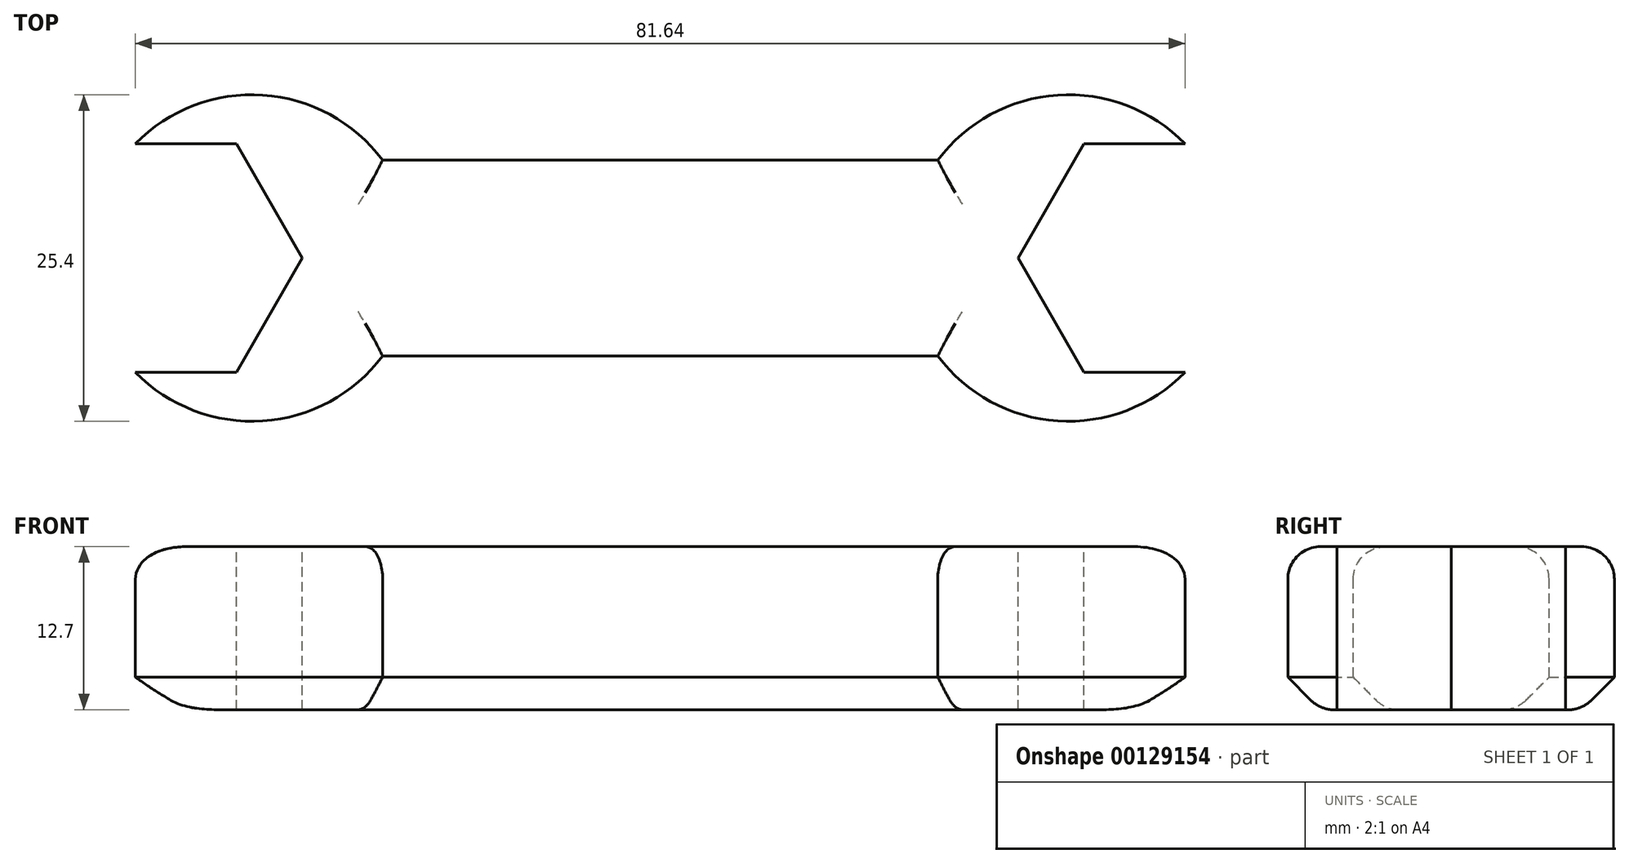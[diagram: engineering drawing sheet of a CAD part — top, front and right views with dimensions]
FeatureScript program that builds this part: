
annotation { "Feature Type Name" : "Feature", "Feature Type Description" : "" }
export const myFeature = defineFeature(function(context is Context, id is Id, definition is map)
    precondition{}
    {
        {
            var Q0;
            Q0=qCreatedBy(makeId("Top.planeOp"),FACE);
            var sketch = newSketch(context, id + "F0", { "sketchPlane" : qUnion([Q0])});
            skArc(sketch, "E0", {"start": v(-21.59, 7.62) * mm, "mid": v(-44.45, 0) * mm, "end": v(-21.59, -7.62) * mm});
            skArc(sketch, "E1", {"start": v(21.59, -7.62) * mm, "mid": v(44.45, 0) * mm, "end": v(21.59, 7.62) * mm});
            skLineSegment(sketch, "E2", {"start": v(-21.59, 7.62) * mm, "end": v(21.59, 7.62) * mm});
            skLineSegment(sketch, "E3", {"start": v(-21.59, -7.62) * mm, "end": v(21.59, -7.62) * mm});
            skLineSegment(sketch, "E4", {"start": v(-31.75, 0) * mm, "end": v(31.75, 0) * mm, "construction": true});
            skSolve(sketch);
        }
        {
            var Q0;
            Q0 = qSketchRegion(id + "F0", true);
            extrude(context, id + "F1", {"entities" : qUnion([Q0]), "endBound" : BoundingType.SYMMETRIC, "oppositeDirection" : true, "depth" : 12.7 * mm});
        }
        {
            var Q0;
            Q0=makeQuery(id+"F1.opExtrude","CAP_FACE",FACE,{"disambiguationData":[OSD([sQuery(id+"F0.wireOp",EDGE,"E0"),sQuery(id+"F0.wireOp",EDGE,"E1"),sQuery(id+"F0.wireOp",EDGE,"E2"),sQuery(id+"F0.wireOp",EDGE,"E3")])],"isStart":true});
            var sketch = newSketch(context, id + "F2", { "sketchPlane" : qUnion([Q0])});
            skCircle(sketch, "E5.cCircle", {"center": v(-38.1, 0) * mm, "radius": 8.9 * mm, "construction": true});
            skLineSegment(sketch, "E5.0", {"start": v(-32.97, 8.9) * mm, "end": v(-27.83, 0) * mm});
            skLineSegment(sketch, "E5.1", {"start": v(-27.83, 0) * mm, "end": v(-32.97, -8.89) * mm});
            skLineSegment(sketch, "E5.2", {"start": v(-32.97, -8.89) * mm, "end": v(-43.23, -8.89) * mm});
            skLineSegment(sketch, "E5.3", {"start": v(-43.23, -8.89) * mm, "end": v(-48.37, 0) * mm});
            skLineSegment(sketch, "E5.4", {"start": v(-48.37, 0) * mm, "end": v(-43.23, 8.89) * mm});
            skLineSegment(sketch, "E5.5", {"start": v(-43.23, 8.89) * mm, "end": v(-32.97, 8.89) * mm});
            skPoint(sketch, "E5.0.midPoint", {"position": v(-29.21, 0) * mm});
            skSolve(sketch);
        }
        {
            var Q0;
            Q0 = qSketchRegion(id + "F2", true);
            extrude(context, id + "F3", {"entities" : qUnion([Q0]), "endBound" : BoundingType.THROUGH_ALL, "oppositeDirection" : true, "depth" : 25.4 * mm});
        }
        {
            var Q0;
            Q0=makeQuery(id+"F3.opExtrude","SWEPT_BODY",BODY,{"disambiguationData":[OSD([sQuery(id+"F2.wireOp",EDGE,"E5.0"),sQuery(id+"F2.wireOp",EDGE,"E5.1"),sQuery(id+"F2.wireOp",EDGE,"E5.2"),sQuery(id+"F2.wireOp",EDGE,"E5.3"),sQuery(id+"F2.wireOp",EDGE,"E5.4"),sQuery(id+"F2.wireOp",EDGE,"E5.5")])]});
            var Q1;
            Q1=qCreatedBy(makeId("Right.planeOp"),FACE);
            mirror(context, id + "F4", {"operationType" : NewBodyOperationType.REMOVE, "entities" : qUnion([Q0]), "mirrorPlane" : qUnion([Q1])});
        }
        {
            var Q0;
            Q0=makeQuery(id+"F3.opExtrude","SWEPT_BODY",BODY,{"disambiguationData":[OSD([sQuery(id+"F2.wireOp",EDGE,"E5.0"),sQuery(id+"F2.wireOp",EDGE,"E5.1"),sQuery(id+"F2.wireOp",EDGE,"E5.2"),sQuery(id+"F2.wireOp",EDGE,"E5.3"),sQuery(id+"F2.wireOp",EDGE,"E5.4"),sQuery(id+"F2.wireOp",EDGE,"E5.5")])]});
            var Q1;
            Q1=makeQuery(id+"F1.opExtrude","SWEPT_BODY",BODY,{"disambiguationData":[OSD([sQuery(id+"F0.wireOp",EDGE,"E0"),sQuery(id+"F0.wireOp",EDGE,"E1"),sQuery(id+"F0.wireOp",EDGE,"E2"),sQuery(id+"F0.wireOp",EDGE,"E3")])]});
            booleanBodies(context, id + "F5", {"operationType" : BooleanOperationType.SUBTRACTION, "tools" : qUnion([Q0]), "targets" : qUnion([Q1])});
        }
        {
            var Q0;
            Q0=makeQuery(id+"F1.opExtrude","CAP_EDGE",EDGE,{"disambiguationData":[OSD([sQuery(id+"F0.wireOp",EDGE,"E3")])],"isStart":true});
            var Q1;
            {var subQ0=sQuery(id+"F0.wireOp",EDGE,"E0");var subQ1=sQuery(id+"F0.wireOp",EDGE,"E3");Q1=makeQuery(id+"F5.opBoolean","SPLIT",EDGE,{"disambiguationData":[TD([makeQuery(id+"F1.opExtrude","SWEPT_FACE",FACE,{"disambiguationData":[OSD([subQ1])]})])],"derivedFrom":makeQuery(id+"F1.opExtrude","CAP_EDGE",EDGE,{"disambiguationData":[OSD([subQ0])],"isStart":true})});}
            var Q2;
            {var subQ0=sQuery(id+"F0.wireOp",EDGE,"E0");var subQ1=sQuery(id+"F0.wireOp",EDGE,"E2");Q2=makeQuery(id+"F5.opBoolean","SPLIT",EDGE,{"disambiguationData":[TD([makeQuery(id+"F1.opExtrude","SWEPT_FACE",FACE,{"disambiguationData":[OSD([subQ1])]})])],"derivedFrom":makeQuery(id+"F1.opExtrude","CAP_EDGE",EDGE,{"disambiguationData":[OSD([subQ0])],"isStart":true})});}
            var Q3;
            Q3=makeQuery(id+"F1.opExtrude","CAP_EDGE",EDGE,{"disambiguationData":[OSD([sQuery(id+"F0.wireOp",EDGE,"E2")])],"isStart":true});
            var Q4;
            {var subQ0=sQuery(id+"F0.wireOp",EDGE,"E2");var subQ1=sQuery(id+"F0.wireOp",EDGE,"E1");Q4=makeQuery(id+"F4.boolean.opBoolean","SPLIT",EDGE,{"disambiguationData":[TD([makeQuery(id+"F1.opExtrude","SWEPT_FACE",FACE,{"disambiguationData":[OSD([subQ0])]})])],"derivedFrom":makeQuery(id+"F1.opExtrude","CAP_EDGE",EDGE,{"disambiguationData":[OSD([subQ1])],"isStart":true})});}
            var Q5;
            {var subQ0=sQuery(id+"F0.wireOp",EDGE,"E3");var subQ1=sQuery(id+"F0.wireOp",EDGE,"E1");Q5=makeQuery(id+"F4.boolean.opBoolean","SPLIT",EDGE,{"disambiguationData":[TD([makeQuery(id+"F1.opExtrude","SWEPT_FACE",FACE,{"disambiguationData":[OSD([subQ0])]})])],"derivedFrom":makeQuery(id+"F1.opExtrude","CAP_EDGE",EDGE,{"disambiguationData":[OSD([subQ1])],"isStart":true})});}
            fillet(context, id + "F6", {"entities" : qUnion([Q0, Q1, Q2, Q3, Q4, Q5]), "radius" : 2.54 * mm, "tangentPropagation" : true, "allowEdgeOverflow" : false});
        }
        {
            var Q0;
            {var subQ0=sQuery(id+"F0.wireOp",EDGE,"E0");var subQ1=sQuery(id+"F0.wireOp",EDGE,"E3");Q0=makeQuery(id+"F5.opBoolean","SPLIT",EDGE,{"disambiguationData":[TD([makeQuery(id+"F1.opExtrude","SWEPT_FACE",FACE,{"disambiguationData":[OSD([subQ1])]})])],"derivedFrom":makeQuery(id+"F1.opExtrude","CAP_EDGE",EDGE,{"disambiguationData":[OSD([subQ0])],"isStart":false})});}
            var Q1;
            Q1=makeQuery(id+"F1.opExtrude","CAP_EDGE",EDGE,{"disambiguationData":[OSD([sQuery(id+"F0.wireOp",EDGE,"E3")])],"isStart":false});
            var Q2;
            {var subQ0=sQuery(id+"F0.wireOp",EDGE,"E3");var subQ1=sQuery(id+"F0.wireOp",EDGE,"E1");Q2=makeQuery(id+"F4.boolean.opBoolean","SPLIT",EDGE,{"disambiguationData":[TD([makeQuery(id+"F1.opExtrude","SWEPT_FACE",FACE,{"disambiguationData":[OSD([subQ0])]})])],"derivedFrom":makeQuery(id+"F1.opExtrude","CAP_EDGE",EDGE,{"disambiguationData":[OSD([subQ1])],"isStart":false})});}
            var Q3;
            {var subQ0=sQuery(id+"F0.wireOp",EDGE,"E2");var subQ1=sQuery(id+"F0.wireOp",EDGE,"E1");Q3=makeQuery(id+"F4.boolean.opBoolean","SPLIT",EDGE,{"disambiguationData":[TD([makeQuery(id+"F1.opExtrude","SWEPT_FACE",FACE,{"disambiguationData":[OSD([subQ0])]})])],"derivedFrom":makeQuery(id+"F1.opExtrude","CAP_EDGE",EDGE,{"disambiguationData":[OSD([subQ1])],"isStart":false})});}
            var Q4;
            Q4=makeQuery(id+"F1.opExtrude","CAP_EDGE",EDGE,{"disambiguationData":[OSD([sQuery(id+"F0.wireOp",EDGE,"E2")])],"isStart":false});
            var Q5;
            {var subQ0=sQuery(id+"F0.wireOp",EDGE,"E0");var subQ1=sQuery(id+"F0.wireOp",EDGE,"E2");Q5=makeQuery(id+"F5.opBoolean","SPLIT",EDGE,{"disambiguationData":[TD([makeQuery(id+"F1.opExtrude","SWEPT_FACE",FACE,{"disambiguationData":[OSD([subQ1])]})])],"derivedFrom":makeQuery(id+"F1.opExtrude","CAP_EDGE",EDGE,{"disambiguationData":[OSD([subQ0])],"isStart":false})});}
            chamfer(context, id + "F7", {"entities" : qUnion([Q0, Q1, Q2, Q3, Q4, Q5]), "width" : 2.54 * mm, "tangentPropagation" : true});
        }
        {
            var Q0;
            {var subQ0=sQuery(id+"F0.wireOp",EDGE,"E3");var subQ1=sQuery(id+"F0.wireOp",EDGE,"E0");var subQ2=makeQuery(id+"F1.opExtrude","CAP_FACE",FACE,{"disambiguationData":[OSD([subQ1,sQuery(id+"F0.wireOp",EDGE,"E1"),sQuery(id+"F0.wireOp",EDGE,"E2"),subQ0])],"isStart":false});Q0=makeQuery(id+"F7.opChamfer","BLEND_EDGE",EDGE,{"blendedFrom":[makeQuery(id+"F5.opBoolean","SPLIT",EDGE,{"disambiguationData":[TD([makeQuery(id+"F1.opExtrude","SWEPT_FACE",FACE,{"disambiguationData":[OSD([subQ0])]})])],"derivedFrom":makeQuery(id+"F1.opExtrude","CAP_EDGE",EDGE,{"disambiguationData":[OSD([subQ1])],"isStart":false})}),subQ2],"blendedInto":[subQ2]});}
            var Q1;
            {var subQ0=sQuery(id+"F0.wireOp",EDGE,"E3");Q1=makeQuery(id+"F7.opChamfer","BLEND_EDGE",EDGE,{"blendedFrom":[makeQuery(id+"F1.opExtrude","CAP_EDGE",EDGE,{"disambiguationData":[OSD([subQ0])],"isStart":false}),makeQuery(id+"F1.opExtrude","CAP_FACE",FACE,{"disambiguationData":[OSD([sQuery(id+"F0.wireOp",EDGE,"E0"),sQuery(id+"F0.wireOp",EDGE,"E1"),sQuery(id+"F0.wireOp",EDGE,"E2"),subQ0])],"isStart":false})],"blendedInto":[makeQuery(id+"F1.opExtrude","CAP_FACE",FACE,{"disambiguationData":[OSD([sQuery(id+"F0.wireOp",EDGE,"E0"),sQuery(id+"F0.wireOp",EDGE,"E1"),sQuery(id+"F0.wireOp",EDGE,"E2"),subQ0])],"isStart":false})]});}
            var Q2;
            {var subQ0=sQuery(id+"F0.wireOp",EDGE,"E3");var subQ1=sQuery(id+"F0.wireOp",EDGE,"E1");var subQ2=makeQuery(id+"F1.opExtrude","CAP_FACE",FACE,{"disambiguationData":[OSD([sQuery(id+"F0.wireOp",EDGE,"E0"),subQ1,sQuery(id+"F0.wireOp",EDGE,"E2"),subQ0])],"isStart":false});Q2=makeQuery(id+"F7.opChamfer","BLEND_EDGE",EDGE,{"blendedFrom":[makeQuery(id+"F4.boolean.opBoolean","SPLIT",EDGE,{"disambiguationData":[TD([makeQuery(id+"F1.opExtrude","SWEPT_FACE",FACE,{"disambiguationData":[OSD([subQ0])]})])],"derivedFrom":makeQuery(id+"F1.opExtrude","CAP_EDGE",EDGE,{"disambiguationData":[OSD([subQ1])],"isStart":false})}),subQ2],"blendedInto":[subQ2]});}
            var Q3;
            {var subQ0=sQuery(id+"F0.wireOp",EDGE,"E2");var subQ1=sQuery(id+"F0.wireOp",EDGE,"E1");var subQ2=makeQuery(id+"F1.opExtrude","CAP_FACE",FACE,{"disambiguationData":[OSD([sQuery(id+"F0.wireOp",EDGE,"E0"),subQ1,subQ0,sQuery(id+"F0.wireOp",EDGE,"E3")])],"isStart":false});Q3=makeQuery(id+"F7.opChamfer","BLEND_EDGE",EDGE,{"blendedFrom":[makeQuery(id+"F4.boolean.opBoolean","SPLIT",EDGE,{"disambiguationData":[TD([makeQuery(id+"F1.opExtrude","SWEPT_FACE",FACE,{"disambiguationData":[OSD([subQ0])]})])],"derivedFrom":makeQuery(id+"F1.opExtrude","CAP_EDGE",EDGE,{"disambiguationData":[OSD([subQ1])],"isStart":false})}),subQ2],"blendedInto":[subQ2]});}
            var Q4;
            {var subQ0=sQuery(id+"F0.wireOp",EDGE,"E2");Q4=makeQuery(id+"F7.opChamfer","BLEND_EDGE",EDGE,{"blendedFrom":[makeQuery(id+"F1.opExtrude","CAP_EDGE",EDGE,{"disambiguationData":[OSD([subQ0])],"isStart":false}),makeQuery(id+"F1.opExtrude","CAP_FACE",FACE,{"disambiguationData":[OSD([sQuery(id+"F0.wireOp",EDGE,"E0"),sQuery(id+"F0.wireOp",EDGE,"E1"),subQ0,sQuery(id+"F0.wireOp",EDGE,"E3")])],"isStart":false})],"blendedInto":[makeQuery(id+"F1.opExtrude","CAP_FACE",FACE,{"disambiguationData":[OSD([sQuery(id+"F0.wireOp",EDGE,"E0"),sQuery(id+"F0.wireOp",EDGE,"E1"),subQ0,sQuery(id+"F0.wireOp",EDGE,"E3")])],"isStart":false})]});}
            var Q5;
            {var subQ0=sQuery(id+"F0.wireOp",EDGE,"E2");var subQ1=sQuery(id+"F0.wireOp",EDGE,"E0");var subQ2=makeQuery(id+"F1.opExtrude","CAP_FACE",FACE,{"disambiguationData":[OSD([subQ1,sQuery(id+"F0.wireOp",EDGE,"E1"),subQ0,sQuery(id+"F0.wireOp",EDGE,"E3")])],"isStart":false});Q5=makeQuery(id+"F7.opChamfer","BLEND_EDGE",EDGE,{"blendedFrom":[makeQuery(id+"F5.opBoolean","SPLIT",EDGE,{"disambiguationData":[TD([makeQuery(id+"F1.opExtrude","SWEPT_FACE",FACE,{"disambiguationData":[OSD([subQ0])]})])],"derivedFrom":makeQuery(id+"F1.opExtrude","CAP_EDGE",EDGE,{"disambiguationData":[OSD([subQ1])],"isStart":false})}),subQ2],"blendedInto":[subQ2]});}
            fillet(context, id + "F8", {"entities" : qUnion([Q0, Q1, Q2, Q3, Q4, Q5]), "radius" : 2.54 * mm, "tangentPropagation" : true, "allowEdgeOverflow" : false});
        }
    });
